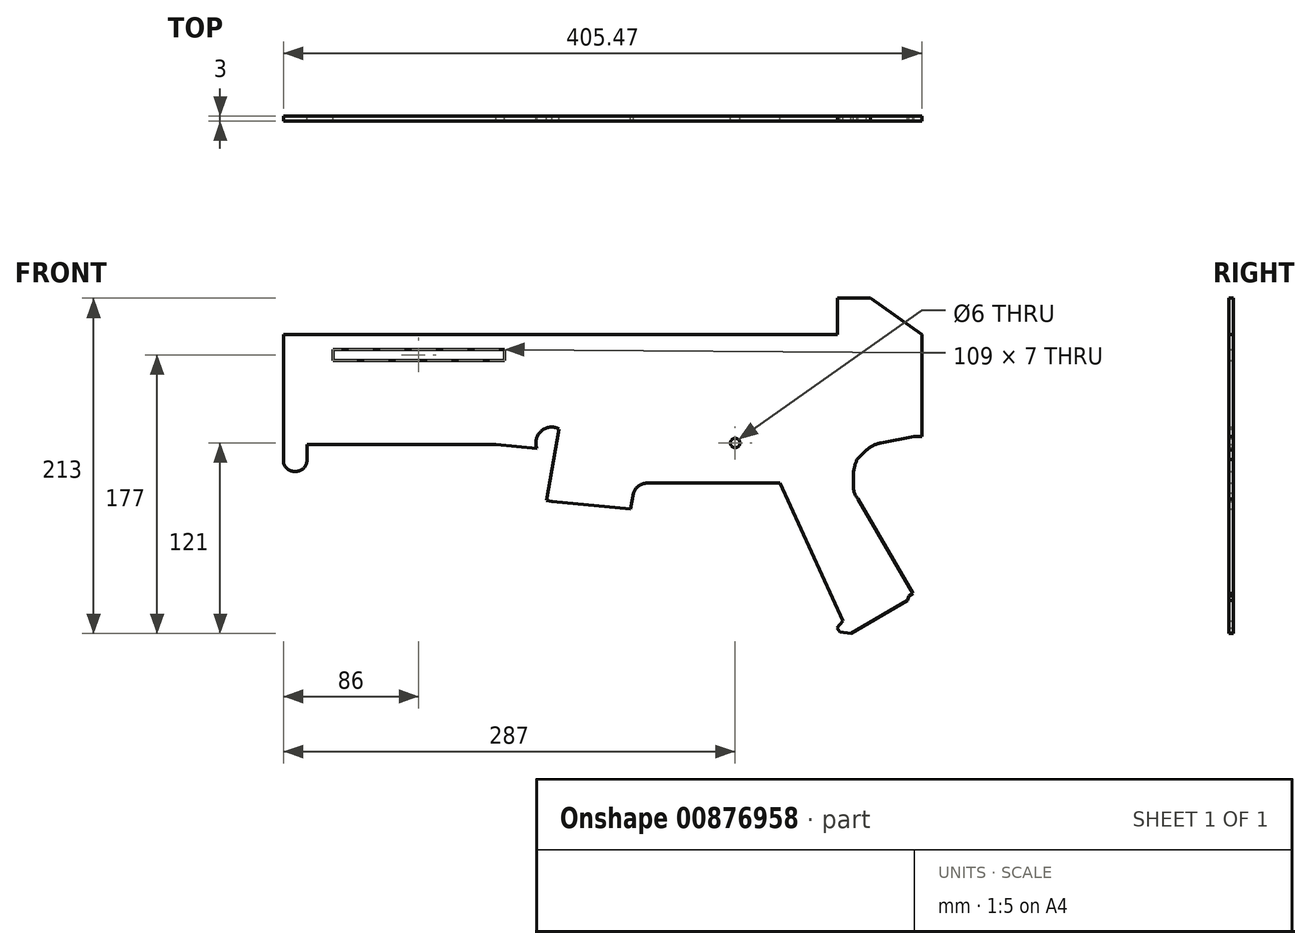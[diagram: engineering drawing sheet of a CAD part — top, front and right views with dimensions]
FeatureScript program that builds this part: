
annotation { "Feature Type Name" : "Feature", "Feature Type Description" : "" }
export const myFeature = defineFeature(function(context is Context, id is Id, definition is map)
    precondition{}
    {
        {
            var Q0;
            Q0=qCreatedBy(makeId("Front.planeOp"),FACE);
            var sketch = newSketch(context, id + "F0", { "sketchPlane" : qUnion([Q0])});
            skLineSegment(sketch, "E0", {"start": v(53.47, -65) * mm, "end": v(53.47, 0) * mm});
            skLineSegment(sketch, "E1", {"start": v(0, 0) * mm, "end": v(-0.03, 23) * mm});
            skLineSegment(sketch, "E2", {"start": v(20.97, 23) * mm, "end": v(53.47, 0) * mm});
            skLineSegment(sketch, "E3", {"start": v(-0.03, 23) * mm, "end": v(20.97, 23) * mm});
            skPoint(sketch, "E4.visualSharp", {"position": v(-0.03, 23) * mm});
            skPoint(sketch, "E5.visualSharp", {"position": v(20.97, 23) * mm});
            skPoint(sketch, "E6.visualSharp", {"position": v(53.47, 0) * mm});
            skPoint(sketch, "E7.visualSharp", {"position": v(0, 0) * mm});
            skLineSegment(sketch, "E8", {"start": v(53.47, -65) * mm, "end": v(48.47, -65) * mm});
            skLineSegment(sketch, "E9", {"start": v(48.47, -65) * mm, "end": v(27.47, -69) * mm});
            skLineSegment(sketch, "E10", {"start": v(18.47, -73.5) * mm, "end": v(12.47, -79.5) * mm});
            skLineSegment(sketch, "E11", {"start": v(9.97, -90.5) * mm, "end": v(9.97, -96.5) * mm});
            skLineSegment(sketch, "E12", {"start": v(12.97, -104.5) * mm, "end": v(47.97, -164.5) * mm});
            skLineSegment(sketch, "E13", {"start": v(47.97, -164.5) * mm, "end": v(45.47, -166) * mm});
            skLineSegment(sketch, "E14", {"start": v(45.47, -166) * mm, "end": v(44.47, -169) * mm});
            skLineSegment(sketch, "E15", {"start": v(44.47, -169) * mm, "end": v(8.47, -190) * mm});
            skLineSegment(sketch, "E16", {"start": v(8.47, -190) * mm, "end": v(1.47, -189) * mm});
            skLineSegment(sketch, "E17", {"start": v(1.47, -189) * mm, "end": v(-0.53, -186.5) * mm});
            skLineSegment(sketch, "E18", {"start": v(-0.53, -186.5) * mm, "end": v(3.47, -182) * mm});
            skLineSegment(sketch, "E19", {"start": v(3.47, -182) * mm, "end": v(-36.5, -94.5) * mm});
            skArc(sketch, "E20", {"start": v(9.97, -90.5) * mm, "mid": v(10.6, -84.86) * mm, "end": v(12.47, -79.5) * mm});
            skArc(sketch, "E21", {"start": v(27.47, -69) * mm, "mid": v(22.65, -70.63) * mm, "end": v(18.47, -73.5) * mm});
            skArc(sketch, "E22", {"start": v(9.97, -96.5) * mm, "mid": v(10.74, -100.77) * mm, "end": v(12.97, -104.5) * mm});
            skLineSegment(sketch, "E23", {"start": v(0, 0) * mm, "end": v(-352, 0) * mm});
            skLineSegment(sketch, "E24", {"start": v(-345, -87) * mm, "end": v(-344, -87) * mm});
            skLineSegment(sketch, "E25", {"start": v(-337, -80) * mm, "end": v(-337, -70) * mm});
            skLineSegment(sketch, "E26", {"start": v(-337, -70) * mm, "end": v(-217, -70) * mm});
            skLineSegment(sketch, "E27", {"start": v(-217, -70) * mm, "end": v(-191, -72.5) * mm});
            skLineSegment(sketch, "E28", {"start": v(-191, -72.5) * mm, "end": v(-179, -72.5) * mm, "construction": true});
            skLineSegment(sketch, "E29", {"start": v(-179, -72.5) * mm, "end": v(-184.82, -105.5) * mm});
            skLineSegment(sketch, "E30", {"start": v(-352, -80) * mm, "end": v(-352, -55.5) * mm});
            skLineSegment(sketch, "E31", {"start": v(-352, 0) * mm, "end": v(-352, -39) * mm});
            skLineSegment(sketch, "E32", {"start": v(-181.32, -106) * mm, "end": v(-184.82, -105.5) * mm});
            skPoint(sketch, "E33", {"position": v(-317, -13) * mm});
            skPoint(sketch, "E34", {"position": v(-215, -13) * mm});
            skLineSegment(sketch, "E35", {"start": v(-97.5, -94.5) * mm, "end": v(-36.5, -94.5) * mm});
            skPoint(sketch, "E36.visualSharp", {"position": v(-352, -87) * mm});
            skArc(sketch, "E36.filletArc", {"start": v(-352, -80) * mm, "mid": v(-349.95, -84.95) * mm, "end": v(-345, -87) * mm});
            skPoint(sketch, "E37.visualSharp", {"position": v(-337, -87) * mm});
            skArc(sketch, "E37.filletArc", {"start": v(-344, -87) * mm, "mid": v(-339.05, -84.95) * mm, "end": v(-337, -80) * mm});
            skPoint(sketch, "E38", {"position": v(-323, -7) * mm});
            skPoint(sketch, "E39", {"position": v(-209, -7) * mm});
            skLineSegment(sketch, "E40.bottom", {"start": v(-320.5, -9.5) * mm, "end": v(-211.5, -9.5) * mm});
            skLineSegment(sketch, "E40.top", {"start": v(-320.5, -16.5) * mm, "end": v(-211.5, -16.5) * mm});
            skLineSegment(sketch, "E40.left", {"start": v(-320.5, -9.5) * mm, "end": v(-320.5, -16.5) * mm});
            skLineSegment(sketch, "E40.right", {"start": v(-211.5, -9.5) * mm, "end": v(-211.5, -16.5) * mm});
            skPoint(sketch, "E41", {"position": v(-121.16, -2.5) * mm});
            skLineSegment(sketch, "E42", {"start": v(-352, -39) * mm, "end": v(-352, -55.5) * mm});
            skLineSegment(sketch, "E43", {"start": v(-181.32, -106) * mm, "end": v(-131.43, -111) * mm});
            skLineSegment(sketch, "E44", {"start": v(-97.5, -94.5) * mm, "end": v(-120.97, -94.5) * mm});
            skLineSegment(sketch, "E45", {"start": v(-131.43, -111) * mm, "end": v(-129.63, -100.8) * mm});
            skArc(sketch, "E46", {"start": v(-120.97, -94.5) * mm, "mid": v(-126.33, -96.24) * mm, "end": v(-129.63, -100.8) * mm});
            skPoint(sketch, "E47", {"position": v(-181.5, -69) * mm});
            skArc(sketch, "E48", {"start": v(-191, -72.5) * mm, "mid": v(-188.18, -61.4) * mm, "end": v(-176.8, -60.03) * mm});
            skLineSegment(sketch, "E49", {"start": v(-179, -72.5) * mm, "end": v(-176.8, -60.03) * mm});
            skCircle(sketch, "E50", {"center": v(-65, -69) * mm, "radius": 3 * mm});
            skSolve(sketch);
        }
        {
            var Q0;
            Q0=qSketchRegion(id+"F0",true);
            var Q1;
            Q1=makeQuery(id+"F0.imprint","IMPRINT",FACE,{"disambiguationData":[TD([[makeQuery(id+"F0.imprint","IMPRINT",EDGE,{"derivedFrom":sQuery(id+"F0.wireOp",EDGE,"7KHTMWfU-3Zso-w6jU-E75I-gNLATLITgT0v.bottom")}),-1.0]])]});
            var Q2;
            Q2=makeQuery(id+"F0.imprint","IMPRINT",FACE,{"disambiguationData":[TD([[makeQuery(id+"F0.imprint","IMPRINT",EDGE,{"derivedFrom":sQuery(id+"F0.wireOp",EDGE,"h5b3wBjq-2nQV-NM1d-5vbp-s6v93ooiL6zY.bottom")}),-1.0]])]});
            extrude(context, id + "F1", {"entities" : qUnion([Q0, Q1, Q2]), "depth" : 3 * mm, "offsetDistance" : 25 * mm});
        }
    });
